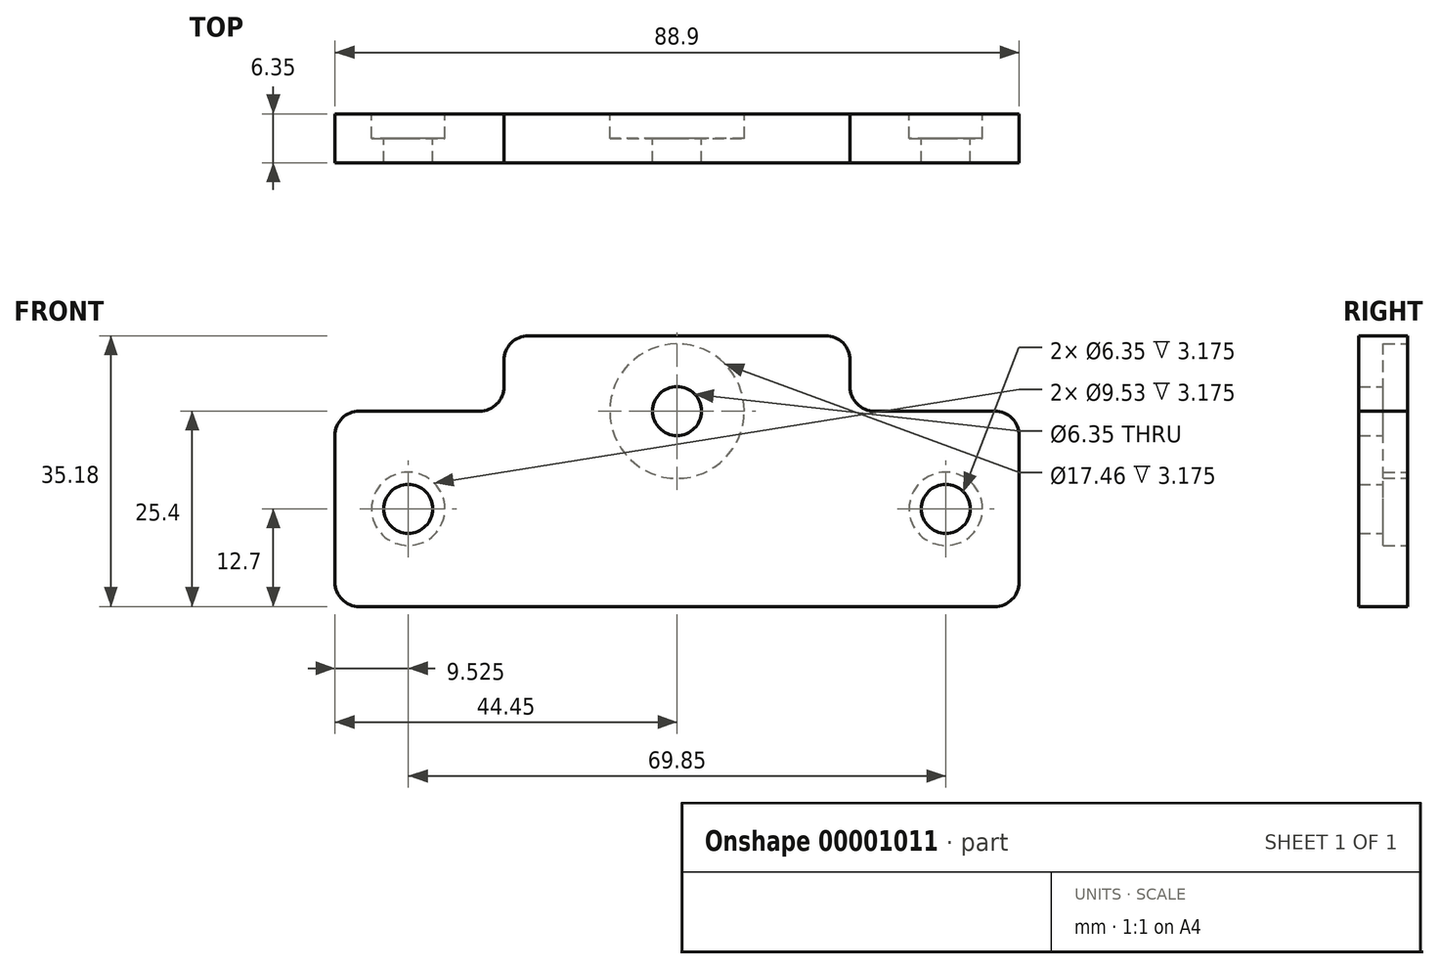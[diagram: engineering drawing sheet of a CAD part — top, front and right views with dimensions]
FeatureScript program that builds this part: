
annotation { "Feature Type Name" : "Feature", "Feature Type Description" : "" }
export const myFeature = defineFeature(function(context is Context, id is Id, definition is map)
    precondition{}
    {
        {
            var Q0;
            Q0=qCreatedBy(makeId("Front.planeOp"),FACE);
            var sketch = newSketch(context, id + "F0", { "sketchPlane" : qUnion([Q0])});
            skLineSegment(sketch, "E0.rect.bottom", {"start": v(-41.28, 12.7) * mm, "end": v(-25.66, 12.7) * mm});
            skLineSegment(sketch, "E0.rect.top", {"start": v(-41.28, -12.7) * mm, "end": v(41.28, -12.7) * mm});
            skLineSegment(sketch, "E0.rect.left", {"start": v(-44.45, 9.53) * mm, "end": v(-44.45, -9.53) * mm});
            skLineSegment(sketch, "E0.rect.right", {"start": v(44.45, 9.53) * mm, "end": v(44.45, -9.53) * mm});
            skPoint(sketch, "E0.rect.middle", {"position": v(0, 0) * mm});
            skCircle(sketch, "E1", {"center": v(-34.93, 0) * mm, "radius": 3.18 * mm});
            skCircle(sketch, "E2", {"center": v(34.93, 0) * mm, "radius": 3.18 * mm});
            skCircle(sketch, "E3", {"center": v(-34.93, 0) * mm, "radius": 4.76 * mm});
            skCircle(sketch, "E4", {"center": v(34.93, 0) * mm, "radius": 4.76 * mm});
            skLineSegment(sketch, "E5.rect.top", {"start": v(19.31, 22.48) * mm, "end": v(-19.31, 22.48) * mm});
            skLineSegment(sketch, "E5.rect.left", {"start": v(22.49, 15.88) * mm, "end": v(22.49, 19.3) * mm});
            skLineSegment(sketch, "E5.rect.right", {"start": v(-22.49, 15.88) * mm, "end": v(-22.49, 19.3) * mm});
            skPoint(sketch, "E5.rect.middle", {"position": v(0, 17.59) * mm});
            skLineSegment(sketch, "E6.trimOffspring", {"start": v(25.66, 12.7) * mm, "end": v(41.28, 12.7) * mm});
            skCircle(sketch, "E7", {"center": v(0, 12.7) * mm, "radius": 8.73 * mm});
            skCircle(sketch, "E8", {"center": v(0, 12.7) * mm, "radius": 3.18 * mm});
            skPoint(sketch, "E9.visualSharp", {"position": v(-22.49, 12.7) * mm});
            skArc(sketch, "E9.filletArc", {"start": v(-25.66, 12.7) * mm, "mid": v(-23.42, 13.63) * mm, "end": v(-22.49, 15.88) * mm});
            skPoint(sketch, "E10.visualSharp", {"position": v(-22.49, 22.48) * mm});
            skArc(sketch, "E10.filletArc", {"start": v(-19.31, 22.48) * mm, "mid": v(-21.56, 21.55) * mm, "end": v(-22.49, 19.3) * mm});
            skPoint(sketch, "E11.visualSharp", {"position": v(22.49, 22.48) * mm});
            skArc(sketch, "E11.filletArc", {"start": v(22.49, 19.3) * mm, "mid": v(21.56, 21.55) * mm, "end": v(19.31, 22.48) * mm});
            skPoint(sketch, "E12.visualSharp", {"position": v(22.49, 12.7) * mm});
            skArc(sketch, "E12.filletArc", {"start": v(22.49, 15.88) * mm, "mid": v(23.42, 13.63) * mm, "end": v(25.66, 12.7) * mm});
            skPoint(sketch, "E13.visualSharp", {"position": v(44.45, 12.7) * mm});
            skArc(sketch, "E13.filletArc", {"start": v(44.45, 9.53) * mm, "mid": v(43.52, 11.77) * mm, "end": v(41.28, 12.7) * mm});
            skPoint(sketch, "E14.visualSharp", {"position": v(44.45, -12.7) * mm});
            skArc(sketch, "E14.filletArc", {"start": v(41.28, -12.7) * mm, "mid": v(43.52, -11.77) * mm, "end": v(44.45, -9.53) * mm});
            skPoint(sketch, "E15.visualSharp", {"position": v(-44.45, -12.7) * mm});
            skArc(sketch, "E15.filletArc", {"start": v(-44.45, -9.53) * mm, "mid": v(-43.52, -11.77) * mm, "end": v(-41.28, -12.7) * mm});
            skPoint(sketch, "E16.visualSharp", {"position": v(-44.45, 12.7) * mm});
            skArc(sketch, "E16.filletArc", {"start": v(-41.28, 12.7) * mm, "mid": v(-43.52, 11.77) * mm, "end": v(-44.45, 9.53) * mm});
            skSolve(sketch);
        }
        {
            var Q0;
            Q0=makeQuery(id+"F0.imprint","IMPRINT",FACE,{"disambiguationData":[TD([[makeQuery(id+"F0.imprint","IMPRINT",EDGE,{"derivedFrom":sQuery(id+"F0.wireOp",EDGE,"E0.rect.bottom")}),-1.0]])]});
            var Q1;
            Q1=makeQuery(id+"F0.imprint","IMPRINT",FACE,{"disambiguationData":[TD([[makeQuery(id+"F0.imprint","IMPRINT",EDGE,{"derivedFrom":sQuery(id+"F0.wireOp",EDGE,"E1")}),-1.0]])]});
            var Q2;
            Q2=makeQuery(id+"F0.imprint","IMPRINT",FACE,{"disambiguationData":[TD([[makeQuery(id+"F0.imprint","IMPRINT",EDGE,{"derivedFrom":sQuery(id+"F0.wireOp",EDGE,"E2")}),-1.0]])]});
            var Q3;
            Q3=makeQuery(id+"F0.imprint","IMPRINT",FACE,{"disambiguationData":[TD([[makeQuery(id+"F0.imprint","IMPRINT",EDGE,{"derivedFrom":sQuery(id+"F0.wireOp",EDGE,"E7")}),1.0]])]});
            extrude(context, id + "F1", {"entities" : qUnion([Q0, Q1, Q2, Q3]), "depth" : 6.35 * mm});
        }
        {
            var Q0;
            Q0=makeQuery(id+"F0.imprint","IMPRINT",FACE,{"disambiguationData":[TD([[makeQuery(id+"F0.imprint","IMPRINT",EDGE,{"derivedFrom":sQuery(id+"F0.wireOp",EDGE,"E7")}),1.0]])]});
            var Q1;
            Q1=makeQuery(id+"F0.imprint","IMPRINT",FACE,{"disambiguationData":[TD([[makeQuery(id+"F0.imprint","IMPRINT",EDGE,{"derivedFrom":sQuery(id+"F0.wireOp",EDGE,"E2")}),-1.0]])]});
            var Q2;
            Q2=makeQuery(id+"F0.imprint","IMPRINT",FACE,{"disambiguationData":[TD([[makeQuery(id+"F0.imprint","IMPRINT",EDGE,{"derivedFrom":sQuery(id+"F0.wireOp",EDGE,"E1")}),-1.0]])]});
            extrude(context, id + "F2", {"entities" : qUnion([Q0, Q1, Q2]), "operationType" : NewBodyOperationType.REMOVE, "depth" : 3.17 * mm});
        }
    });
